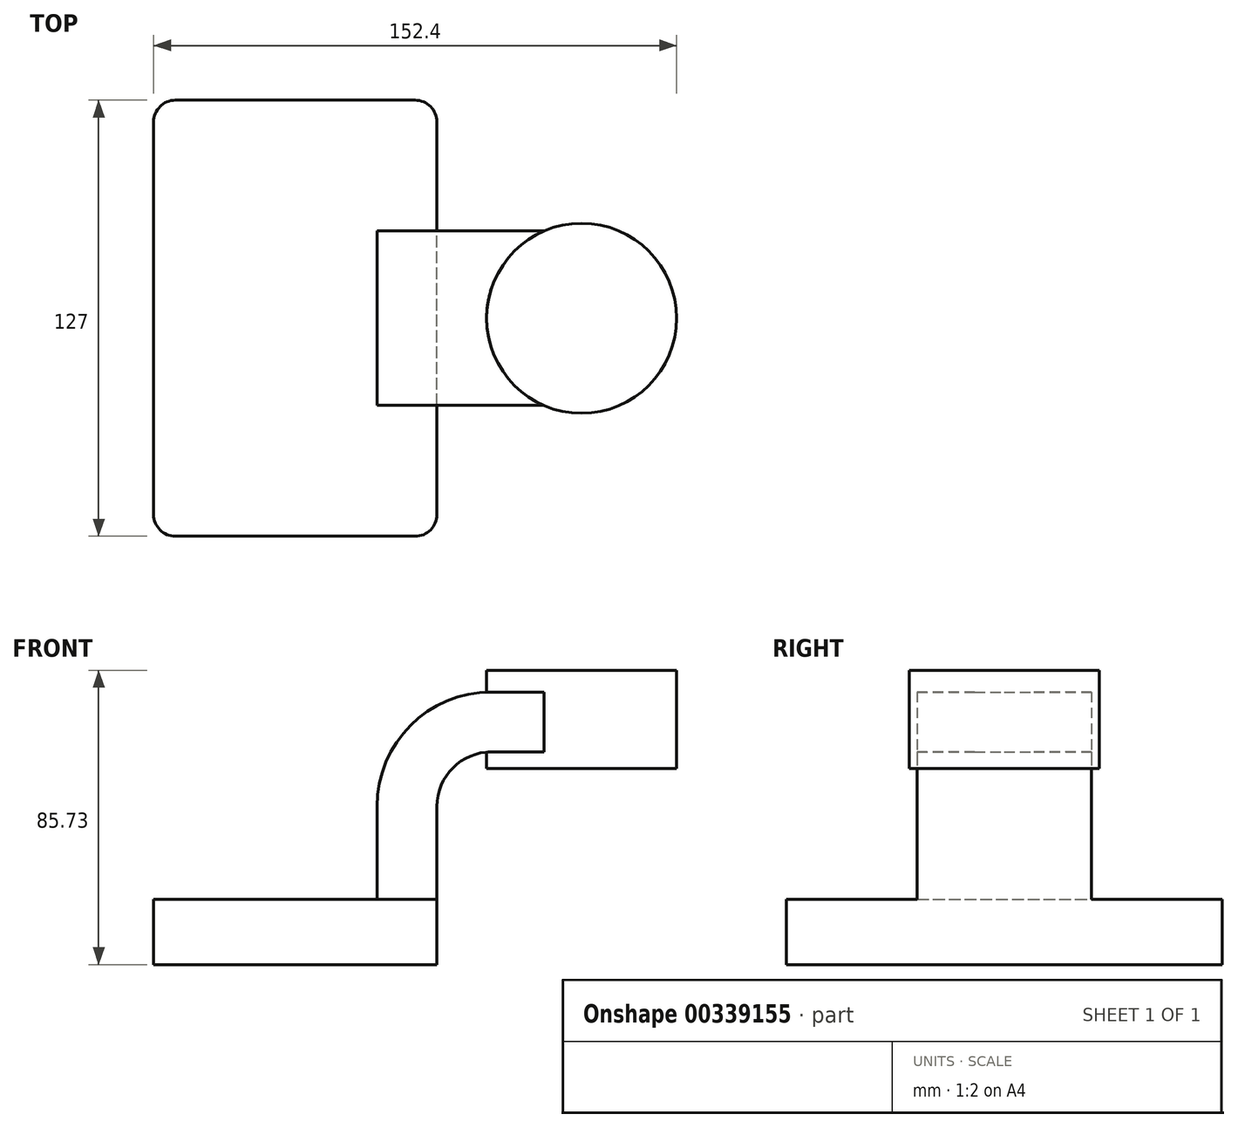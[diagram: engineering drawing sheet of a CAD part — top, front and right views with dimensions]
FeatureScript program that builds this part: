
annotation { "Feature Type Name" : "Feature", "Feature Type Description" : "" }
export const myFeature = defineFeature(function(context is Context, id is Id, definition is map)
    precondition{}
    {
        {
            var Q0;
            Q0=qCreatedBy(makeId("Front.planeOp"),FACE);
            var sketch = newSketch(context, id + "F0", { "sketchPlane" : qUnion([Q0])});
            skLineSegment(sketch, "E0.bottom", {"start": v(-41.28, 9.52) * mm, "end": v(41.27, 9.53) * mm});
            skLineSegment(sketch, "E0.top", {"start": v(-41.28, -9.53) * mm, "end": v(41.28, -9.53) * mm});
            skLineSegment(sketch, "E0.left", {"start": v(-41.28, 9.52) * mm, "end": v(-41.27, -9.53) * mm});
            skLineSegment(sketch, "E0.right", {"start": v(41.28, 9.53) * mm, "end": v(41.28, -9.52) * mm});
            skPoint(sketch, "E0.middle", {"position": v(0, 0) * mm});
            skLineSegment(sketch, "E1", {"start": v(41.27, 9.53) * mm, "end": v(41.27, 36.53) * mm});
            skArc(sketch, "E2", {"start": v(41.27, 36.53) * mm, "mid": v(45.92, 47.75) * mm, "end": v(57.15, 52.4) * mm});
            skLineSegment(sketch, "E3", {"start": v(57.15, 52.4) * mm, "end": v(83.45, 52.4) * mm});
            skLineSegment(sketch, "E4.bottom", {"start": v(111.12, 47.62) * mm, "end": v(60.32, 47.62) * mm});
            skLineSegment(sketch, "E4.top", {"start": v(111.12, 76.2) * mm, "end": v(60.32, 76.2) * mm});
            skLineSegment(sketch, "E4.left", {"start": v(111.12, 47.62) * mm, "end": v(111.12, 76.2) * mm});
            skLineSegment(sketch, "E4.right", {"start": v(60.32, 47.62) * mm, "end": v(60.32, 76.2) * mm});
            skPoint(sketch, "E4.middle", {"position": v(85.72, 61.91) * mm});
            skLineSegment(sketch, "E5.0", {"start": v(57.15, 69.86) * mm, "end": v(83.45, 69.86) * mm});
            skArc(sketch, "E5.1", {"start": v(23.82, 36.53) * mm, "mid": v(33.58, 60.1) * mm, "end": v(57.15, 69.86) * mm});
            skLineSegment(sketch, "E5.2", {"start": v(23.82, 9.53) * mm, "end": v(23.82, 36.53) * mm});
            skLineSegment(sketch, "E6", {"start": v(83.45, 47.62) * mm, "end": v(83.45, 76.2) * mm});
            skFitSpline(sketch, "E7", {"points": [v(-41.27, 9.52) * mm, v(57.15, 69.86) * mm], "startDerivative": vector(19.08, 86.67) * mm, "endDerivative": vector(108.77, -0.8) * mm});
            skSolve(sketch);
        }
        {
            var Q0;
            Q0=makeQuery(id+"F0.imprint","IMPRINT",FACE,{"disambiguationData":[TD([[makeQuery(id+"F0.imprint","IMPRINT",EDGE,{"derivedFrom":sQuery(id+"F0.wireOp",EDGE,"E0.top")}),1.0]])]});
            extrude(context, id + "F1", {"entities" : qUnion([Q0]), "endBound" : BoundingType.SYMMETRIC, "depth" : 127 * mm});
        }
        {
            var Q0;
            {var subQ0=sQuery(id+"F0.wireOp",EDGE,"E6");var subQ1=sQuery(id+"F0.wireOp",EDGE,"E3");var subQ2=makeQuery(id+"F0.imprint","INTERSECT",VERTEX,{"derivedFrom":[subQ1,subQ0]});Q0=makeQuery(id+"F0.imprint","IMPRINT",FACE,{"disambiguationData":[TD([[makeQuery(id+"F0.imprint","IMPRINT",EDGE,{"disambiguationData":[TD([[subQ2,1.0]])],"derivedFrom":subQ1}),1.0]])]});}
            var Q1;
            {var subQ4=sQuery(id+"F0.wireOp",EDGE,"E1");Q1=makeQuery(id+"F0.imprint","IMPRINT",FACE,{"disambiguationData":[TD([[makeQuery(id+"F0.imprint","IMPRINT",EDGE,{"derivedFrom":subQ4}),1.0]])]});}
            extrude(context, id + "F2", {"entities" : qUnion([Q0, Q1]), "operationType" : NewBodyOperationType.ADD, "endBound" : BoundingType.SYMMETRIC, "depth" : 50.8 * mm});
        }
        {
            var Q0;
            Q0=makeQuery(id+"F0.imprint","IMPRINT",FACE,{"disambiguationData":[TD([[makeQuery(id+"F0.imprint","IMPRINT",EDGE,{"derivedFrom":sQuery(id+"F0.wireOp",EDGE,"E5.1")}),1.0]])]});
            extrude(context, id + "F3", {"entities" : qUnion([Q0]), "operationType" : NewBodyOperationType.ADD, "endBound" : BoundingType.SYMMETRIC, "depth" : 15.88 * mm});
        }
        {
            var Q0;
            {var subQ0=sQuery(id+"F0.wireOp",EDGE,"E4.left");Q0=makeQuery(id+"F0.imprint","IMPRINT",FACE,{"disambiguationData":[TD([[makeQuery(id+"F0.imprint","IMPRINT",EDGE,{"derivedFrom":subQ0}),1.0]])]});}
            var Q1;
            Q1=sQuery(id+"F0.wireOp",EDGE,"E6");
            revolve(context, id + "F4", {"operationType" : NewBodyOperationType.ADD, "entities" : qUnion([Q0]), "axis" : qUnion([Q1]), "revolveType" : RevolveType.FULL});
        }
        {
            var Q0;
            Q0=makeQuery(id+"F1.opExtrude","CAP_EDGE",EDGE,{"disambiguationData":[OSD([sQuery(id+"F0.wireOp",EDGE,"E0.left")])],"isStart":false});
            var Q1;
            Q1=makeQuery(id+"F1.opExtrude","CAP_EDGE",EDGE,{"disambiguationData":[OSD([sQuery(id+"F0.wireOp",EDGE,"E0.right")])],"isStart":false});
            var Q2;
            Q2=makeQuery(id+"F1.opExtrude","CAP_EDGE",EDGE,{"disambiguationData":[OSD([sQuery(id+"F0.wireOp",EDGE,"E0.right")])],"isStart":true});
            var Q3;
            Q3=makeQuery(id+"F1.opExtrude","CAP_EDGE",EDGE,{"disambiguationData":[OSD([sQuery(id+"F0.wireOp",EDGE,"E0.left")])],"isStart":true});
            fillet(context, id + "F5", {"entities" : qUnion([Q0, Q1, Q2, Q3]), "radius" : 6.35 * mm, "tangentPropagation" : true, "allowEdgeOverflow" : false});
        }
    });
